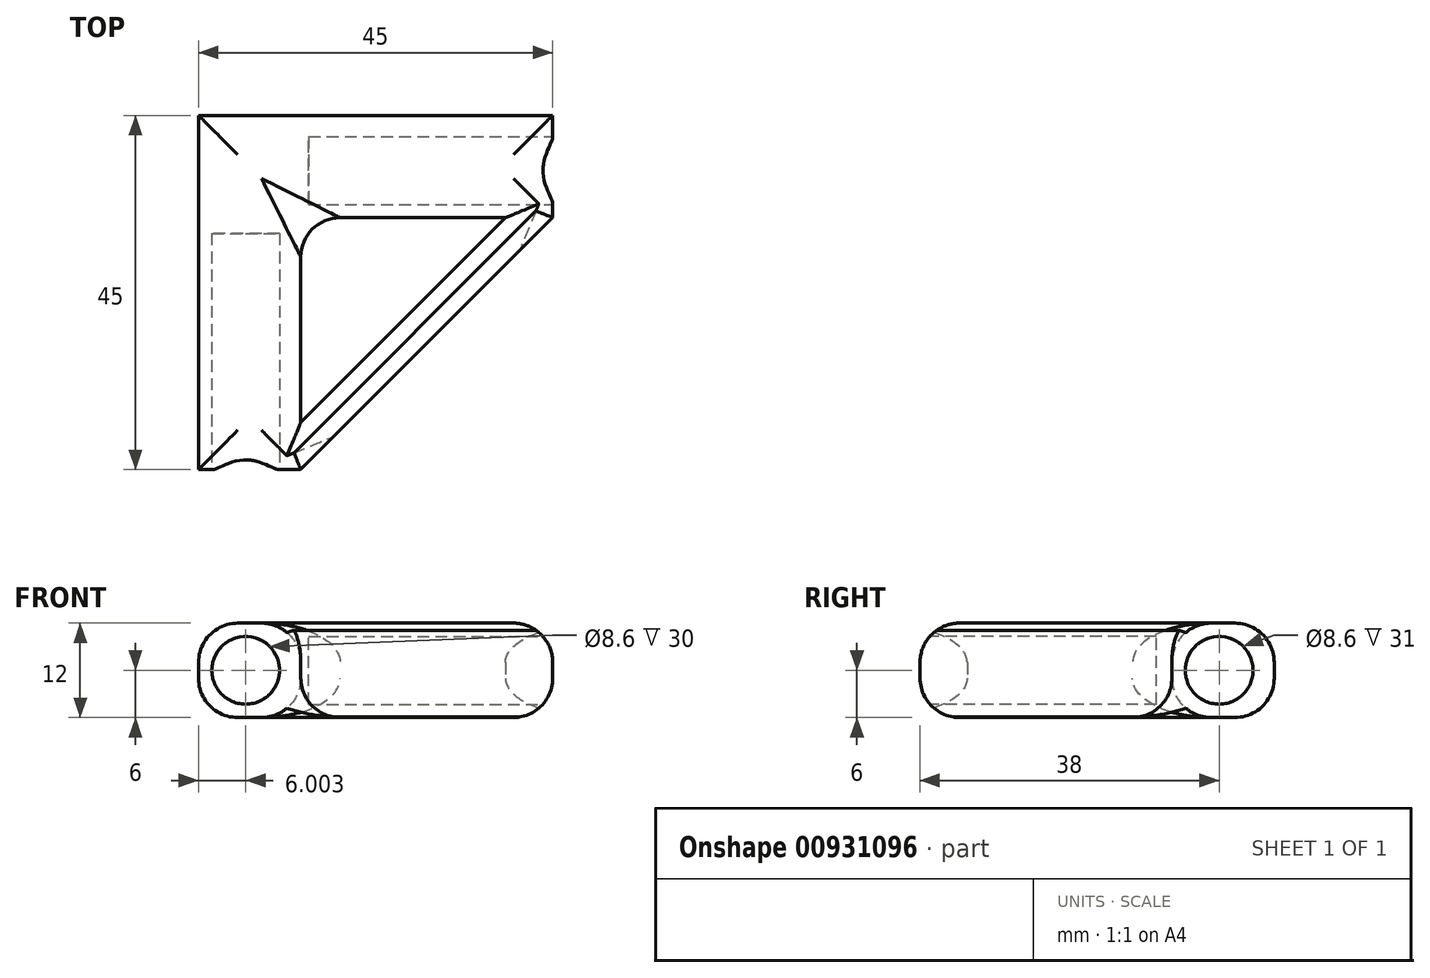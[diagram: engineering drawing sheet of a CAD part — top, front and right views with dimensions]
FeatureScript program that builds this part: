
annotation { "Feature Type Name" : "Feature", "Feature Type Description" : "" }
export const myFeature = defineFeature(function(context is Context, id is Id, definition is map)
    precondition{}
    {
        {
            var Q0;
            Q0=qCreatedBy(makeId("Top.planeOp"),FACE);
            var sketch = newSketch(context, id + "F0", { "sketchPlane" : qUnion([Q0])});
            skLineSegment(sketch, "E0.bottom", {"start": v(-37.32, 13) * mm, "end": v(7.68, 13) * mm});
            skLineSegment(sketch, "E0.top", {"start": v(-37.32, 0) * mm, "end": v(7.68, 0) * mm});
            skLineSegment(sketch, "E0.left", {"start": v(-37.32, 13) * mm, "end": v(-37.32, 0) * mm});
            skLineSegment(sketch, "E0.right", {"start": v(7.68, 13) * mm, "end": v(7.68, 0) * mm});
            skLineSegment(sketch, "E1.bottom", {"start": v(-37.32, 0) * mm, "end": v(-24.32, 0) * mm});
            skLineSegment(sketch, "E1.top", {"start": v(-37.32, -32) * mm, "end": v(-24.32, -32) * mm});
            skLineSegment(sketch, "E1.left", {"start": v(-37.32, 0) * mm, "end": v(-37.32, -32) * mm});
            skLineSegment(sketch, "E1.right", {"start": v(-24.32, 0) * mm, "end": v(-24.32, -32) * mm});
            skLineSegment(sketch, "E2", {"start": v(7.68, 0) * mm, "end": v(-24.32, -32) * mm});
            skLineSegment(sketch, "E3", {"start": v(-24.32, -26) * mm, "end": v(1.68, 0) * mm});
            skSolve(sketch);
        }
        {
            var Q0;
            {var subQ5=sQuery(id+"F0.wireOp",EDGE,"E1.top");var subQ9=sQuery(id+"F0.wireOp",EDGE,"E2");Q0=qUnion([makeQuery(id+"F0.imprint","IMPRINT",FACE,{"disambiguationData":[TD([[makeQuery(id+"F0.imprint","IMPRINT",EDGE,{"derivedFrom":subQ9}),-1.0]])]}),makeQuery(id+"F0.imprint","IMPRINT",FACE,{"disambiguationData":[TD([[makeQuery(id+"F0.imprint","IMPRINT",EDGE,{"derivedFrom":sQuery(id+"F0.wireOp",EDGE,"E0.bottom")}),-1.0]])]}),makeQuery(id+"F0.imprint","IMPRINT",FACE,{"disambiguationData":[TD([[makeQuery(id+"F0.imprint","IMPRINT",EDGE,{"derivedFrom":subQ5}),1.0]])]})]);}
            extrude(context, id + "F1", {"entities" : qUnion([Q0]), "depth" : 12 * mm, "offsetDistance" : 25 * mm});
        }
        {
            var Q0;
            Q0=makeQuery(id+"F1.opExtrude","SWEPT_FACE",FACE,{"disambiguationData":[OSD([sQuery(id+"F0.wireOp",EDGE,"E1.top")])]});
            var sketch = newSketch(context, id + "F2", { "sketchPlane" : qUnion([Q0])});
            skCircle(sketch, "E4", {"center": v(-31.32, 6) * mm, "radius": 4.3 * mm});
            skSolve(sketch);
        }
        {
            var Q0;
            Q0=makeQuery(id+"F2.imprint","IMPRINT",FACE,{"disambiguationData":[TD([[makeQuery(id+"F2.imprint","IMPRINT",EDGE,{"derivedFrom":sQuery(id+"F2.wireOp",EDGE,"E4")}),1.0]])]});
            extrude(context, id + "F3", {"entities" : qUnion([Q0]), "operationType" : NewBodyOperationType.REMOVE, "oppositeDirection" : true, "depth" : 30 * mm, "offsetDistance" : 25 * mm});
        }
        {
            var Q0;
            Q0=makeQuery(id+"F1.opExtrude","SWEPT_FACE",FACE,{"disambiguationData":[OSD([sQuery(id+"F0.wireOp",EDGE,"E0.right")])]});
            var sketch = newSketch(context, id + "F4", { "sketchPlane" : qUnion([Q0])});
            skCircle(sketch, "E5", {"center": v(6, 6) * mm, "radius": 4.3 * mm});
            skSolve(sketch);
        }
        {
            var Q0;
            Q0=makeQuery(id+"F4.imprint","IMPRINT",FACE,{"disambiguationData":[TD([[makeQuery(id+"F4.imprint","IMPRINT",EDGE,{"derivedFrom":sQuery(id+"F4.wireOp",EDGE,"E5")}),1.0]])]});
            extrude(context, id + "F5", {"entities" : qUnion([Q0]), "operationType" : NewBodyOperationType.REMOVE, "oppositeDirection" : true, "depth" : 31 * mm, "offsetDistance" : 25 * mm});
        }
        {
            var Q0;
            Q0=makeQuery(id+"F1.opExtrude","CAP_EDGE",EDGE,{"disambiguationData":[OSD([sQuery(id+"F0.wireOp",EDGE,"E0.bottom")])],"isStart":false});
            var Q1;
            Q1=makeQuery(id+"F1.opExtrude","CAP_EDGE",EDGE,{"disambiguationData":[OSD([sQuery(id+"F0.wireOp",EDGE,"E0.left"),sQuery(id+"F0.wireOp",EDGE,"E1.left")])],"isStart":false});
            var Q2;
            Q2=makeQuery(id+"F1.opExtrude","CAP_EDGE",EDGE,{"disambiguationData":[OSD([sQuery(id+"F0.wireOp",EDGE,"E0.bottom")])],"isStart":true});
            var Q3;
            Q3=makeQuery(id+"F1.opExtrude","CAP_EDGE",EDGE,{"disambiguationData":[OSD([sQuery(id+"F0.wireOp",EDGE,"E0.left"),sQuery(id+"F0.wireOp",EDGE,"E1.left")])],"isStart":true});
            var Q4;
            Q4=makeQuery(id+"F1.opExtrude","CAP_EDGE",EDGE,{"disambiguationData":[OSD([sQuery(id+"F0.wireOp",EDGE,"E1.right")])],"isStart":true});
            var Q5;
            Q5=makeQuery(id+"F1.opExtrude","CAP_EDGE",EDGE,{"disambiguationData":[OSD([sQuery(id+"F0.wireOp",EDGE,"E0.top")])],"isStart":true});
            var Q6;
            Q6=makeQuery(id+"F1.opExtrude","CAP_EDGE",EDGE,{"disambiguationData":[OSD([sQuery(id+"F0.wireOp",EDGE,"E3")])],"isStart":true});
            var Q7;
            Q7=makeQuery(id+"F1.opExtrude","CAP_EDGE",EDGE,{"disambiguationData":[OSD([sQuery(id+"F0.wireOp",EDGE,"E2")])],"isStart":false});
            var Q8;
            Q8=makeQuery(id+"F1.opExtrude","CAP_FACE",FACE,{"disambiguationData":[OSD([sQuery(id+"F0.wireOp",EDGE,"E0.bottom"),sQuery(id+"F0.wireOp",EDGE,"E0.top"),sQuery(id+"F0.wireOp",EDGE,"E0.left"),sQuery(id+"F0.wireOp",EDGE,"E0.right"),sQuery(id+"F0.wireOp",EDGE,"E1.top"),sQuery(id+"F0.wireOp",EDGE,"E1.left"),sQuery(id+"F0.wireOp",EDGE,"E1.right"),sQuery(id+"F0.wireOp",EDGE,"E2"),sQuery(id+"F0.wireOp",EDGE,"E3")])],"isStart":false});
            fillet(context, id + "F6", {"entities" : qUnion([Q0, Q1, Q2, Q3, Q4, Q5, Q6, Q7, Q8]), "radius" : 5 * mm, "tangentPropagation" : true, "allowEdgeOverflow" : false});
        }
        {
            var Q0;
            Q0=makeQuery(id+"F1.opExtrude","SWEPT_EDGE",EDGE,{"disambiguationData":[OSD([sQuery(id+"F0.wireOp",EDGE,"E0.top"),sQuery(id+"F0.wireOp",EDGE,"E1.right")])]});
            fillet(context, id + "F7", {"entities" : qUnion([Q0]), "radius" : 5 * mm, "tangentPropagation" : true, "allowEdgeOverflow" : false});
        }
        {
            var Q0;
            Q0=makeQuery(id+"F1.opExtrude","CAP_EDGE",EDGE,{"disambiguationData":[OSD([sQuery(id+"F0.wireOp",EDGE,"E2")])],"isStart":true});
            var Q1;
            {var subQ0=sQuery(id+"F0.wireOp",EDGE,"E1.left");var subQ1=sQuery(id+"F0.wireOp",EDGE,"E0.left");Q1=makeQuery(id+"F6.opFillet","BLEND_EDGE",EDGE,{"blendedFrom":[makeQuery(id+"F1.opExtrude","CAP_EDGE",EDGE,{"disambiguationData":[OSD([subQ1,subQ0])],"isStart":true}),makeQuery(id+"F1.opExtrude","CAP_FACE",FACE,{"disambiguationData":[OSD([sQuery(id+"F0.wireOp",EDGE,"E0.bottom"),sQuery(id+"F0.wireOp",EDGE,"E0.top"),subQ1,sQuery(id+"F0.wireOp",EDGE,"E0.right"),sQuery(id+"F0.wireOp",EDGE,"E1.top"),subQ0,sQuery(id+"F0.wireOp",EDGE,"E1.right"),sQuery(id+"F0.wireOp",EDGE,"E2"),sQuery(id+"F0.wireOp",EDGE,"E3")])],"isStart":true})],"blendedInto":[makeQuery(id+"F1.opExtrude","CAP_FACE",FACE,{"disambiguationData":[OSD([sQuery(id+"F0.wireOp",EDGE,"E0.bottom"),sQuery(id+"F0.wireOp",EDGE,"E0.top"),subQ1,sQuery(id+"F0.wireOp",EDGE,"E0.right"),sQuery(id+"F0.wireOp",EDGE,"E1.top"),subQ0,sQuery(id+"F0.wireOp",EDGE,"E1.right"),sQuery(id+"F0.wireOp",EDGE,"E2"),sQuery(id+"F0.wireOp",EDGE,"E3")])],"isStart":true})]});}
            var Q2;
            {var subQ0=sQuery(id+"F0.wireOp",EDGE,"E0.bottom");Q2=makeQuery(id+"F6.opFillet","BLEND_EDGE",EDGE,{"blendedFrom":[makeQuery(id+"F1.opExtrude","CAP_EDGE",EDGE,{"disambiguationData":[OSD([subQ0])],"isStart":true}),makeQuery(id+"F1.opExtrude","CAP_FACE",FACE,{"disambiguationData":[OSD([subQ0,sQuery(id+"F0.wireOp",EDGE,"E0.top"),sQuery(id+"F0.wireOp",EDGE,"E0.left"),sQuery(id+"F0.wireOp",EDGE,"E0.right"),sQuery(id+"F0.wireOp",EDGE,"E1.top"),sQuery(id+"F0.wireOp",EDGE,"E1.left"),sQuery(id+"F0.wireOp",EDGE,"E1.right"),sQuery(id+"F0.wireOp",EDGE,"E2"),sQuery(id+"F0.wireOp",EDGE,"E3")])],"isStart":true})],"blendedInto":[makeQuery(id+"F1.opExtrude","CAP_FACE",FACE,{"disambiguationData":[OSD([subQ0,sQuery(id+"F0.wireOp",EDGE,"E0.top"),sQuery(id+"F0.wireOp",EDGE,"E0.left"),sQuery(id+"F0.wireOp",EDGE,"E0.right"),sQuery(id+"F0.wireOp",EDGE,"E1.top"),sQuery(id+"F0.wireOp",EDGE,"E1.left"),sQuery(id+"F0.wireOp",EDGE,"E1.right"),sQuery(id+"F0.wireOp",EDGE,"E2"),sQuery(id+"F0.wireOp",EDGE,"E3")])],"isStart":true})]});}
            var Q3;
            Q3=makeQuery(id+"F1.opExtrude","CAP_FACE",FACE,{"disambiguationData":[OSD([sQuery(id+"F0.wireOp",EDGE,"E0.bottom"),sQuery(id+"F0.wireOp",EDGE,"E0.top"),sQuery(id+"F0.wireOp",EDGE,"E0.left"),sQuery(id+"F0.wireOp",EDGE,"E0.right"),sQuery(id+"F0.wireOp",EDGE,"E1.top"),sQuery(id+"F0.wireOp",EDGE,"E1.left"),sQuery(id+"F0.wireOp",EDGE,"E1.right"),sQuery(id+"F0.wireOp",EDGE,"E2"),sQuery(id+"F0.wireOp",EDGE,"E3")])],"isStart":true});
            fillet(context, id + "F8", {"entities" : qUnion([Q0, Q1, Q2, Q3]), "radius" : 5 * mm, "allowEdgeOverflow" : false});
        }
    });
